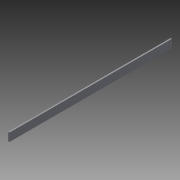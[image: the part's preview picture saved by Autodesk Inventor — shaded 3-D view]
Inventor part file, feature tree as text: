
AUTODESK INVENTOR PART (.ipt)
format: ipt  version: 2015 SP1 (Build 190203100, 203)  size: 77,824 bytes
history: native  units: mm
features: other x3, sketch x1
ambient origin geometry x8: Origin, YZ Plane, XZ Plane, XY Plane, X Axis, Y Axis, Z Axis, Center Point
bodies: Solid1 (feature_tree)
feature tree (4):
  other  "Miroir.ipt"
  other  "Solid1::Miroir.ipt"
  other  "TaggingFeature1"
  sketch  "Sketch1"  dims[d0=10.0mm]
